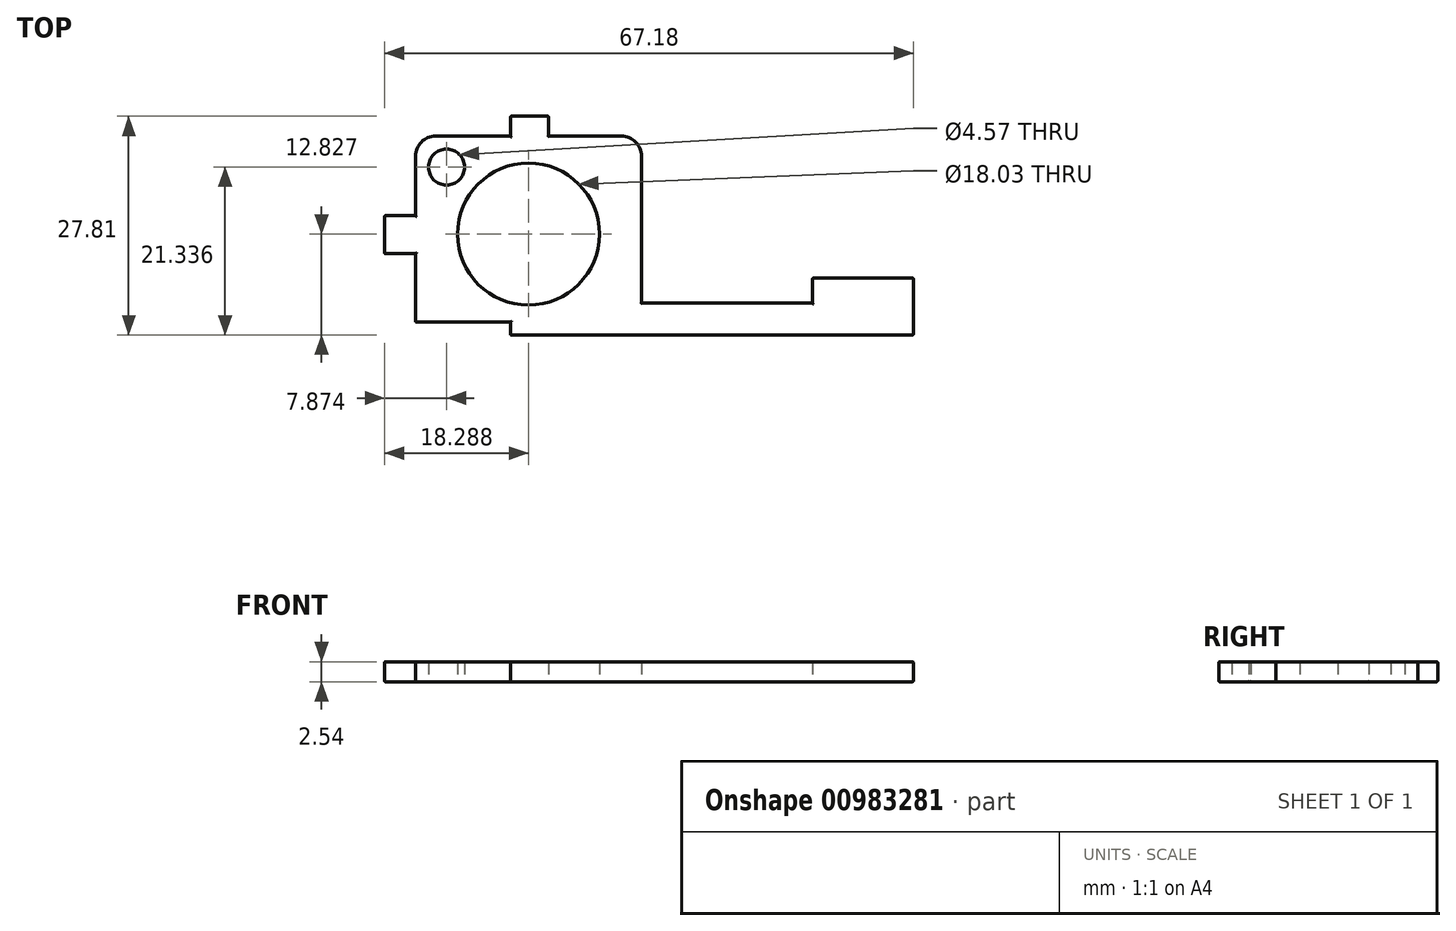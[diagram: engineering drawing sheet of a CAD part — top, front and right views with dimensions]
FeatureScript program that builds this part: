
annotation { "Feature Type Name" : "Feature", "Feature Type Description" : "" }
export const myFeature = defineFeature(function(context is Context, id is Id, definition is map)
    precondition{}
    {
        {
            var Q0;
            Q0=qCreatedBy(makeId("Top.planeOp"),FACE);
            var sketch = newSketch(context, id + "F0", { "sketchPlane" : qUnion([Q0])});
            skLineSegment(sketch, "E0.bottom", {"start": v(0, 0) * mm, "end": v(67.18, 0) * mm, "construction": true});
            skLineSegment(sketch, "E0.top", {"start": v(0, 27.81) * mm, "end": v(67.18, 27.81) * mm, "construction": true});
            skLineSegment(sketch, "E0.left", {"start": v(0, 0) * mm, "end": v(0, 27.81) * mm, "construction": true});
            skLineSegment(sketch, "E0.right", {"start": v(67.18, 0) * mm, "end": v(67.18, 27.81) * mm, "construction": true});
            skLineSegment(sketch, "E1", {"start": v(0, 1.65) * mm, "end": v(67.18, 1.65) * mm, "construction": true});
            skLineSegment(sketch, "E2", {"start": v(0, 25.27) * mm, "end": v(67.18, 25.27) * mm, "construction": true});
            skLineSegment(sketch, "E3", {"start": v(3.94, 27.81) * mm, "end": v(3.94, 0) * mm, "construction": true});
            skLineSegment(sketch, "E4", {"start": v(0, 4.06) * mm, "end": v(67.18, 4.06) * mm, "construction": true});
            skLineSegment(sketch, "E5", {"start": v(0, 7.24) * mm, "end": v(67.18, 7.24) * mm, "construction": true});
            skLineSegment(sketch, "E6", {"start": v(32.64, 27.81) * mm, "end": v(32.64, 0) * mm, "construction": true});
            skLineSegment(sketch, "E7", {"start": v(16, 0) * mm, "end": v(16, 27.81) * mm, "construction": true});
            skLineSegment(sketch, "E8", {"start": v(54.36, 27.81) * mm, "end": v(54.36, 0) * mm, "construction": true});
            skLineSegment(sketch, "E9", {"start": v(20.83, 27.81) * mm, "end": v(20.83, 0) * mm, "construction": true});
            skLineSegment(sketch, "E10", {"start": v(3.94, 21.84) * mm, "end": v(32.64, 21.84) * mm, "construction": true});
            skLineSegment(sketch, "E11", {"start": v(27.3, 25.27) * mm, "end": v(27.3, 4.06) * mm, "construction": true});
            skCircle(sketch, "E12", {"center": v(18.29, 12.83) * mm, "radius": 9.02 * mm, "construction": true});
            skLineSegment(sketch, "E13", {"start": v(3.94, 3.8) * mm, "end": v(32.64, 3.81) * mm, "construction": true});
            skCircle(sketch, "E14", {"center": v(7.87, 21.34) * mm, "radius": 2.29 * mm, "construction": true});
            skLineSegment(sketch, "E15", {"start": v(0, 10.34) * mm, "end": v(3.94, 10.34) * mm, "construction": true});
            skLineSegment(sketch, "E16", {"start": v(0, 15.16) * mm, "end": v(3.94, 15.16) * mm, "construction": true});
            skSolve(sketch);
        }
        {
            var Q0;
            Q0=qCreatedBy(makeId("Top.planeOp"),FACE);
            var sketch = newSketch(context, id + "F1", { "sketchPlane" : qUnion([Q0])});
            skLineSegment(sketch, "E17", {"start": v(16, 0) * mm, "end": v(16, 1.65) * mm});
            skLineSegment(sketch, "E18", {"start": v(16, 1.65) * mm, "end": v(3.94, 1.65) * mm});
            skLineSegment(sketch, "E19", {"start": v(3.94, 1.65) * mm, "end": v(3.94, 10.34) * mm});
            skLineSegment(sketch, "E20", {"start": v(3.94, 10.34) * mm, "end": v(0, 10.34) * mm});
            skLineSegment(sketch, "E21", {"start": v(0, 10.34) * mm, "end": v(0, 15.16) * mm});
            skLineSegment(sketch, "E22", {"start": v(0, 15.16) * mm, "end": v(3.94, 15.16) * mm});
            skLineSegment(sketch, "E23", {"start": v(3.94, 15.16) * mm, "end": v(3.94, 25.27) * mm});
            skLineSegment(sketch, "E24", {"start": v(3.94, 25.27) * mm, "end": v(16, 25.27) * mm});
            skLineSegment(sketch, "E25", {"start": v(16, 25.27) * mm, "end": v(16, 27.81) * mm});
            skLineSegment(sketch, "E26", {"start": v(16, 27.81) * mm, "end": v(20.83, 27.81) * mm});
            skLineSegment(sketch, "E27", {"start": v(20.83, 27.81) * mm, "end": v(20.83, 25.27) * mm});
            skLineSegment(sketch, "E28", {"start": v(20.83, 25.27) * mm, "end": v(32.64, 25.27) * mm});
            skLineSegment(sketch, "E29", {"start": v(32.64, 25.27) * mm, "end": v(32.64, 4.06) * mm});
            skLineSegment(sketch, "E30", {"start": v(32.64, 4.06) * mm, "end": v(54.36, 4.06) * mm});
            skLineSegment(sketch, "E31", {"start": v(54.36, 4.06) * mm, "end": v(54.36, 7.24) * mm});
            skLineSegment(sketch, "E32", {"start": v(54.36, 7.24) * mm, "end": v(67.18, 7.24) * mm});
            skLineSegment(sketch, "E33", {"start": v(67.18, 7.24) * mm, "end": v(67.18, 0) * mm});
            skLineSegment(sketch, "E34", {"start": v(67.18, 0) * mm, "end": v(16, 0) * mm});
            skCircle(sketch, "E35.0", {"center": v(7.87, 21.34) * mm, "radius": 2.29 * mm});
            skCircle(sketch, "E36.0", {"center": v(18.29, 12.83) * mm, "radius": 9.02 * mm});
            skSolve(sketch);
        }
        {
            var Q0;
            Q0=makeQuery(id+"F1.imprint","IMPRINT",FACE,{"disambiguationData":[TD([[makeQuery(id+"F1.imprint","IMPRINT",EDGE,{"derivedFrom":sQuery(id+"F1.wireOp",EDGE,"E17")}),-1.0]])]});
            extrude(context, id + "F2", {"entities" : qUnion([Q0]), "depth" : 2.54 * mm, "offsetDistance" : 25.4 * mm});
        }
        {
            var Q0;
            Q0=makeQuery(id+"F2.opExtrude","SWEPT_EDGE",EDGE,{"disambiguationData":[OSD([sQuery(id+"F1.wireOp",EDGE,"E23"),sQuery(id+"F1.wireOp",EDGE,"E24")])]});
            var Q1;
            Q1=makeQuery(id+"F2.opExtrude","SWEPT_EDGE",EDGE,{"disambiguationData":[OSD([sQuery(id+"F1.wireOp",EDGE,"E28"),sQuery(id+"F1.wireOp",EDGE,"E29")])]});
            fillet(context, id + "F3", {"entities" : qUnion([Q0, Q1]), "radius" : 2.54 * mm, "tangentPropagation" : true, "allowEdgeOverflow" : false});
        }
        {
            var Q0;
            Q0=makeQuery(id+"F2.opExtrude","CAP_FACE",FACE,{"disambiguationData":[OSD([sQuery(id+"F1.wireOp",EDGE,"E17"),sQuery(id+"F1.wireOp",EDGE,"E18"),sQuery(id+"F1.wireOp",EDGE,"E19"),sQuery(id+"F1.wireOp",EDGE,"E20"),sQuery(id+"F1.wireOp",EDGE,"E21"),sQuery(id+"F1.wireOp",EDGE,"E22"),sQuery(id+"F1.wireOp",EDGE,"E23"),sQuery(id+"F1.wireOp",EDGE,"E24"),sQuery(id+"F1.wireOp",EDGE,"E25"),sQuery(id+"F1.wireOp",EDGE,"E26"),sQuery(id+"F1.wireOp",EDGE,"E27"),sQuery(id+"F1.wireOp",EDGE,"E28"),sQuery(id+"F1.wireOp",EDGE,"E29"),sQuery(id+"F1.wireOp",EDGE,"E30"),sQuery(id+"F1.wireOp",EDGE,"E31"),sQuery(id+"F1.wireOp",EDGE,"E32"),sQuery(id+"F1.wireOp",EDGE,"E33"),sQuery(id+"F1.wireOp",EDGE,"E34"),sQuery(id+"F1.wireOp",EDGE,"E35.0"),sQuery(id+"F1.wireOp",EDGE,"E36.0")])],"isStart":false});
            var Q1;
            Q1=makeQuery(id+"F2.opExtrude","CAP_FACE",FACE,{"disambiguationData":[OSD([sQuery(id+"F1.wireOp",EDGE,"E17"),sQuery(id+"F1.wireOp",EDGE,"E18"),sQuery(id+"F1.wireOp",EDGE,"E19"),sQuery(id+"F1.wireOp",EDGE,"E20"),sQuery(id+"F1.wireOp",EDGE,"E21"),sQuery(id+"F1.wireOp",EDGE,"E22"),sQuery(id+"F1.wireOp",EDGE,"E23"),sQuery(id+"F1.wireOp",EDGE,"E24"),sQuery(id+"F1.wireOp",EDGE,"E25"),sQuery(id+"F1.wireOp",EDGE,"E26"),sQuery(id+"F1.wireOp",EDGE,"E27"),sQuery(id+"F1.wireOp",EDGE,"E28"),sQuery(id+"F1.wireOp",EDGE,"E29"),sQuery(id+"F1.wireOp",EDGE,"E30"),sQuery(id+"F1.wireOp",EDGE,"E31"),sQuery(id+"F1.wireOp",EDGE,"E32"),sQuery(id+"F1.wireOp",EDGE,"E33"),sQuery(id+"F1.wireOp",EDGE,"E34"),sQuery(id+"F1.wireOp",EDGE,"E35.0"),sQuery(id+"F1.wireOp",EDGE,"E36.0")])],"isStart":true});
            var Q2;
            Q2=makeQuery(id+"F2.opExtrude","SWEPT_EDGE",EDGE,{"disambiguationData":[OSD([sQuery(id+"F1.wireOp",EDGE,"E26"),sQuery(id+"F1.wireOp",EDGE,"E27")])]});
            var Q3;
            Q3=makeQuery(id+"F2.opExtrude","SWEPT_EDGE",EDGE,{"disambiguationData":[OSD([sQuery(id+"F1.wireOp",EDGE,"E25"),sQuery(id+"F1.wireOp",EDGE,"E26")])]});
            var Q4;
            Q4=makeQuery(id+"F2.opExtrude","SWEPT_EDGE",EDGE,{"disambiguationData":[OSD([sQuery(id+"F1.wireOp",EDGE,"E21"),sQuery(id+"F1.wireOp",EDGE,"E22")])]});
            var Q5;
            Q5=makeQuery(id+"F2.opExtrude","SWEPT_EDGE",EDGE,{"disambiguationData":[OSD([sQuery(id+"F1.wireOp",EDGE,"E20"),sQuery(id+"F1.wireOp",EDGE,"E21")])]});
            var Q6;
            Q6=makeQuery(id+"F2.opExtrude","SWEPT_EDGE",EDGE,{"disambiguationData":[OSD([sQuery(id+"F1.wireOp",EDGE,"E18"),sQuery(id+"F1.wireOp",EDGE,"E19")])]});
            var Q7;
            Q7=makeQuery(id+"F2.opExtrude","SWEPT_EDGE",EDGE,{"disambiguationData":[OSD([sQuery(id+"F1.wireOp",EDGE,"E17"),sQuery(id+"F1.wireOp",EDGE,"E34")])]});
            var Q8;
            Q8=makeQuery(id+"F2.opExtrude","SWEPT_EDGE",EDGE,{"disambiguationData":[OSD([sQuery(id+"F1.wireOp",EDGE,"E31"),sQuery(id+"F1.wireOp",EDGE,"E32")])]});
            var Q9;
            Q9=makeQuery(id+"F2.opExtrude","SWEPT_EDGE",EDGE,{"disambiguationData":[OSD([sQuery(id+"F1.wireOp",EDGE,"E32"),sQuery(id+"F1.wireOp",EDGE,"E33")])]});
            var Q10;
            Q10=makeQuery(id+"F2.opExtrude","SWEPT_EDGE",EDGE,{"disambiguationData":[OSD([sQuery(id+"F1.wireOp",EDGE,"E33"),sQuery(id+"F1.wireOp",EDGE,"E34")])]});
            fillet(context, id + "F4", {"entities" : qUnion([Q0, Q1, Q2, Q3, Q4, Q5, Q6, Q7, Q8, Q9, Q10]), "radius" : 0.13 * mm, "tangentPropagation" : true, "allowEdgeOverflow" : false});
        }
    });
